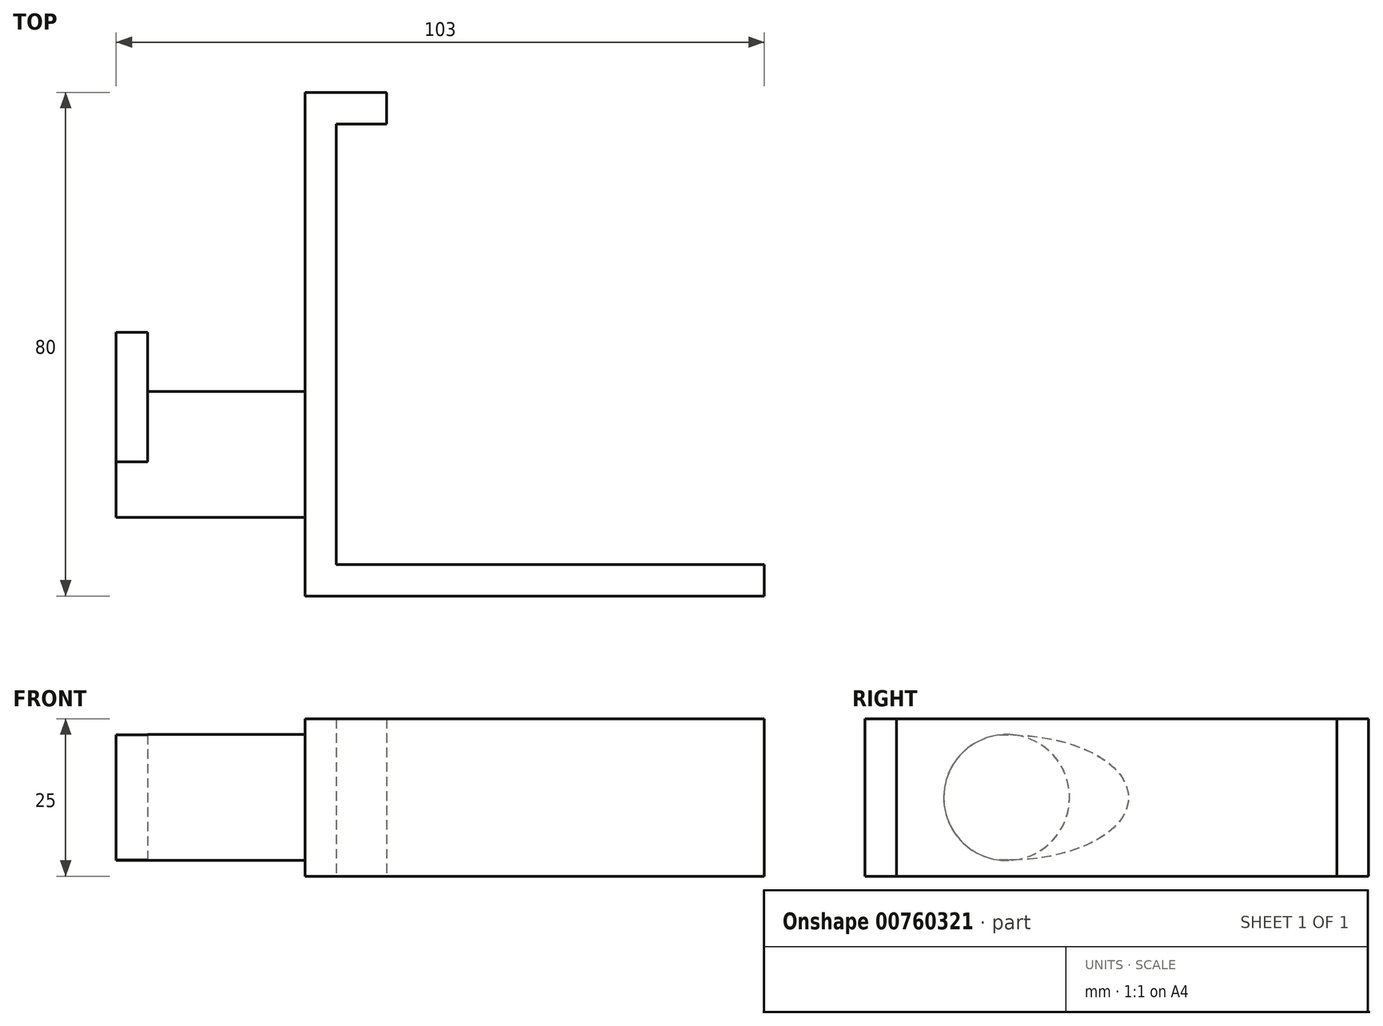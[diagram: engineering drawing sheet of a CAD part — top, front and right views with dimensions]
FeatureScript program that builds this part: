
annotation { "Feature Type Name" : "Feature", "Feature Type Description" : "" }
export const myFeature = defineFeature(function(context is Context, id is Id, definition is map)
    precondition{}
    {
        {
            var Q0;
            Q0=qCreatedBy(makeId("Top.planeOp"),FACE);
            var sketch = newSketch(context, id + "F0", { "sketchPlane" : qUnion([Q0])});
            skLineSegment(sketch, "E0", {"start": v(-9.65, 19.82) * mm, "end": v(3.35, 19.82) * mm});
            skLineSegment(sketch, "E1", {"start": v(3.35, 19.82) * mm, "end": v(3.35, 14.82) * mm});
            skLineSegment(sketch, "E2", {"start": v(3.35, 14.82) * mm, "end": v(-4.65, 14.82) * mm});
            skLineSegment(sketch, "E3", {"start": v(-4.65, 14.82) * mm, "end": v(-4.65, -55.18) * mm});
            skLineSegment(sketch, "E4", {"start": v(-4.65, -55.18) * mm, "end": v(63.35, -55.18) * mm});
            skLineSegment(sketch, "E5", {"start": v(63.35, -55.18) * mm, "end": v(63.35, -60.18) * mm});
            skLineSegment(sketch, "E6", {"start": v(63.35, -60.18) * mm, "end": v(-9.65, -60.18) * mm});
            skLineSegment(sketch, "E7", {"start": v(-9.65, -60.18) * mm, "end": v(-9.65, 19.82) * mm});
            skSolve(sketch);
        }
        {
            var Q0;
            Q0 = qSketchRegion(id + "F0", true);
            extrude(context, id + "F1", {"entities" : qUnion([Q0]), "endBound" : BoundingType.SYMMETRIC, "depth" : 25 * mm, "offsetDistance" : 25 * mm});
        }
        {
            var Q0;
            Q0=makeQuery(id+"F1.opExtrude","SWEPT_FACE",FACE,{"disambiguationData":[OSD([sQuery(id+"F0.wireOp",EDGE,"E7")])]});
            var sketch = newSketch(context, id + "F2", { "sketchPlane" : qUnion([Q0])});
            skLineSegment(sketch, "E8", {"start": v(60.18, -12.5) * mm, "end": v(35.18, -12.5) * mm, "construction": true});
            skLineSegment(sketch, "E9", {"start": v(35.18, -12.5) * mm, "end": v(60.18, 12.5) * mm, "construction": true});
            skCircle(sketch, "E10", {"center": v(47.68, 0) * mm, "radius": 10 * mm});
            skCircle(sketch, "E11", {"center": v(37.68, 0) * mm, "radius": 10 * mm});
            skSolve(sketch);
        }
        {
            var Q0;
            {var subQ0=sQuery(id+"F2.wireOp",EDGE,"E11");var subQ1=sQuery(id+"F2.wireOp",EDGE,"E10");var subQ2=makeQuery(id+"F2.imprint","INTERSECT",VERTEX,{"disambiguationData":[OD(0.0)],"derivedFrom":[subQ1,subQ0]});Q0=makeQuery(id+"F2.imprint","IMPRINT",FACE,{"disambiguationData":[TD([[makeQuery(id+"F2.imprint","IMPRINT",EDGE,{"disambiguationData":[TD([[subQ2,1.0]])],"derivedFrom":subQ1}),-1.0]])]});}
            var Q1;
            {var subQ0=sQuery(id+"F2.wireOp",EDGE,"E11");var subQ1=sQuery(id+"F2.wireOp",EDGE,"E10");var subQ2=makeQuery(id+"F2.imprint","INTERSECT",VERTEX,{"disambiguationData":[OD(0.0)],"derivedFrom":[subQ1,subQ0]});Q1=makeQuery(id+"F2.imprint","IMPRINT",FACE,{"disambiguationData":[TD([[makeQuery(id+"F2.imprint","IMPRINT",EDGE,{"disambiguationData":[TD([[subQ2,1.0]])],"derivedFrom":subQ1}),1.0]])]});}
            extrude(context, id + "F3", {"entities" : qUnion([Q0, Q1]), "depth" : 25 * mm, "offsetDistance" : 25 * mm});
        }
        {
            var Q0;
            Q0=makeQuery(id+"F3.opExtrude","CAP_FACE",FACE,{"disambiguationData":[OSD([sQuery(id+"F2.wireOp",EDGE,"E11")])],"isStart":false});
            var sketch = newSketch(context, id + "F4", { "sketchPlane" : qUnion([Q0])});
            skLineSegment(sketch, "E12", {"start": v(34.9, 9.6) * mm, "end": v(40.11, -9.7) * mm, "construction": true});
            skLineSegment(sketch, "E13", {"start": v(40.11, -9.7) * mm, "end": v(37.5, 0) * mm, "construction": true});
            skEllipse(sketch, "E14", {"center": v(37.5, 0) * mm, "majorRadius": 19.2 * mm, "minorRadius": 9.95 * mm, "majorAxis": v(-1, 0)});
            skSolve(sketch);
        }
        {
            var Q0;
            {var subQ0=sQuery(id+"F4.wireOp",EDGE,"E14");var subQ1=makeQuery(id+"F3.opExtrude","CAP_EDGE",EDGE,{"disambiguationData":[OSD([sQuery(id+"F2.wireOp",EDGE,"E11")])],"isStart":false});var subQ2=makeQuery(id+"F4.imprint","INTERSECT",VERTEX,{"disambiguationData":[OD(1.0)],"derivedFrom":[subQ1,subQ0]});Q0=makeQuery(id+"F4.imprint","IMPRINT",FACE,{"disambiguationData":[TD([[makeQuery(id+"F4.imprint","IMPRINT",EDGE,{"disambiguationData":[TD([[subQ2,1.0]])],"derivedFrom":subQ0}),1.0]])]});}
            var Q1;
            {var subQ0=sQuery(id+"F4.wireOp",EDGE,"E14");var subQ1=makeQuery(id+"F3.opExtrude","CAP_EDGE",EDGE,{"disambiguationData":[OSD([sQuery(id+"F2.wireOp",EDGE,"E11")])],"isStart":false});var subQ2=makeQuery(id+"F4.imprint","INTERSECT",VERTEX,{"disambiguationData":[OD(0.0)],"derivedFrom":[subQ1,subQ0]});Q1=makeQuery(id+"F4.imprint","IMPRINT",FACE,{"disambiguationData":[TD([[makeQuery(id+"F4.imprint","IMPRINT",EDGE,{"disambiguationData":[TD([[subQ2,1.0]])],"derivedFrom":subQ0}),1.0]])]});}
            extrude(context, id + "F5", {"entities" : qUnion([Q0, Q1]), "operationType" : NewBodyOperationType.ADD, "depth" : 5 * mm, "offsetDistance" : 25 * mm});
        }
    });
